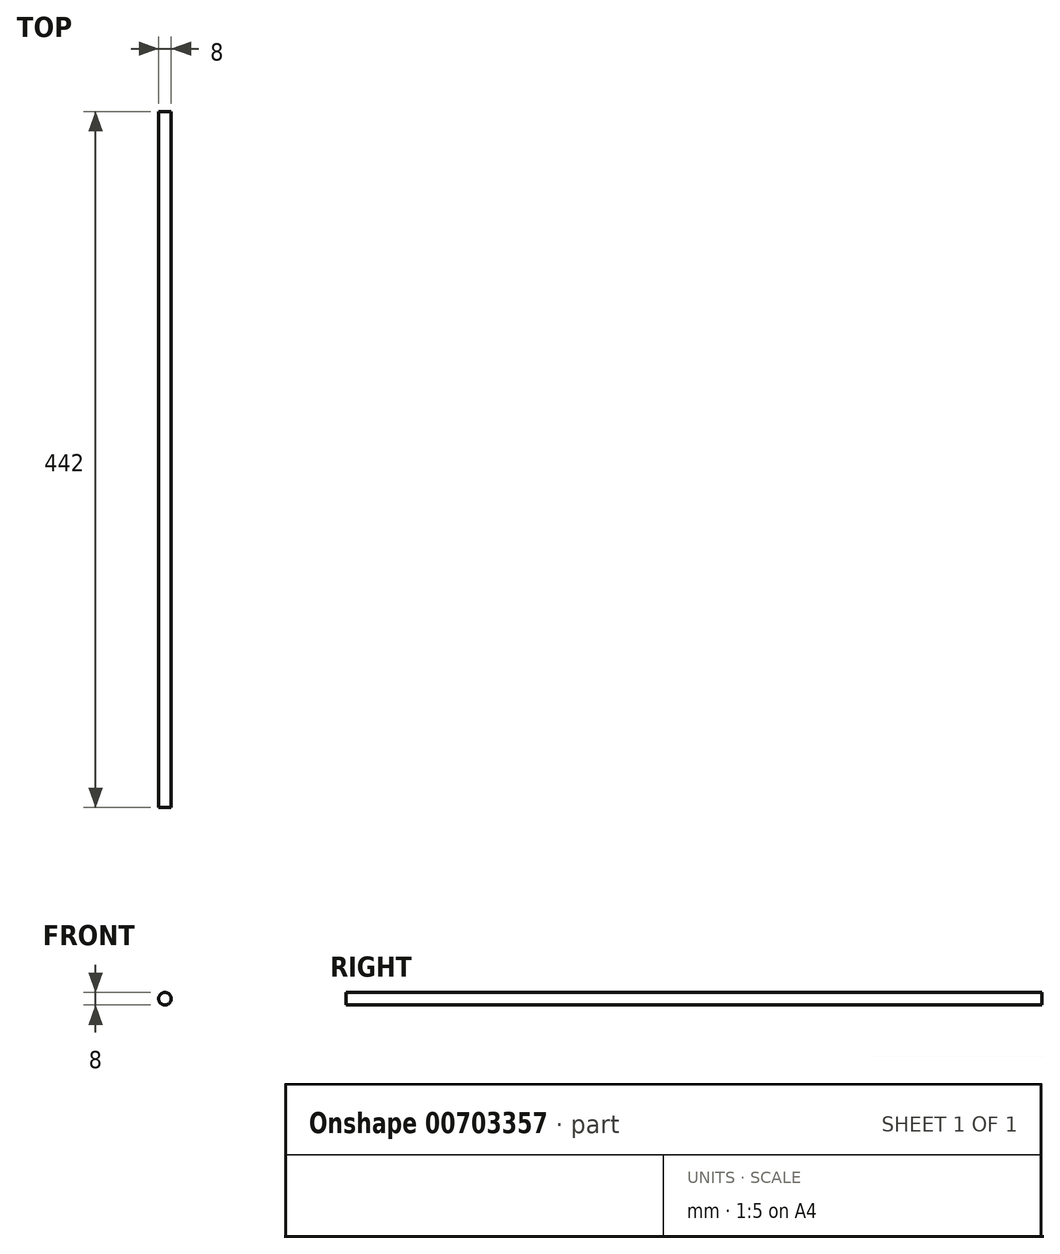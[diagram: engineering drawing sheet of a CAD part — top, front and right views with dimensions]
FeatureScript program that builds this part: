
annotation { "Feature Type Name" : "Feature", "Feature Type Description" : "" }
export const myFeature = defineFeature(function(context is Context, id is Id, definition is map)
    precondition{}
    {
        {
            var Q0;
            Q0=qCreatedBy(makeId("Front.planeOp"),FACE);
            var sketch = newSketch(context, id + "F0", { "sketchPlane" : qUnion([Q0])});
            skCircle(sketch, "E0", {"center": v(0, 0) * mm, "radius": 4 * mm});
            skSolve(sketch);
        }
        {
            var Q0;
            Q0 = qSketchRegion(id + "F0", true);
            extrude(context, id + "F1", {"entities" : qUnion([Q0]), "oppositeDirection" : true, "depth" : 442 * mm, "offsetDistance" : 25 * mm});
        }
    });
